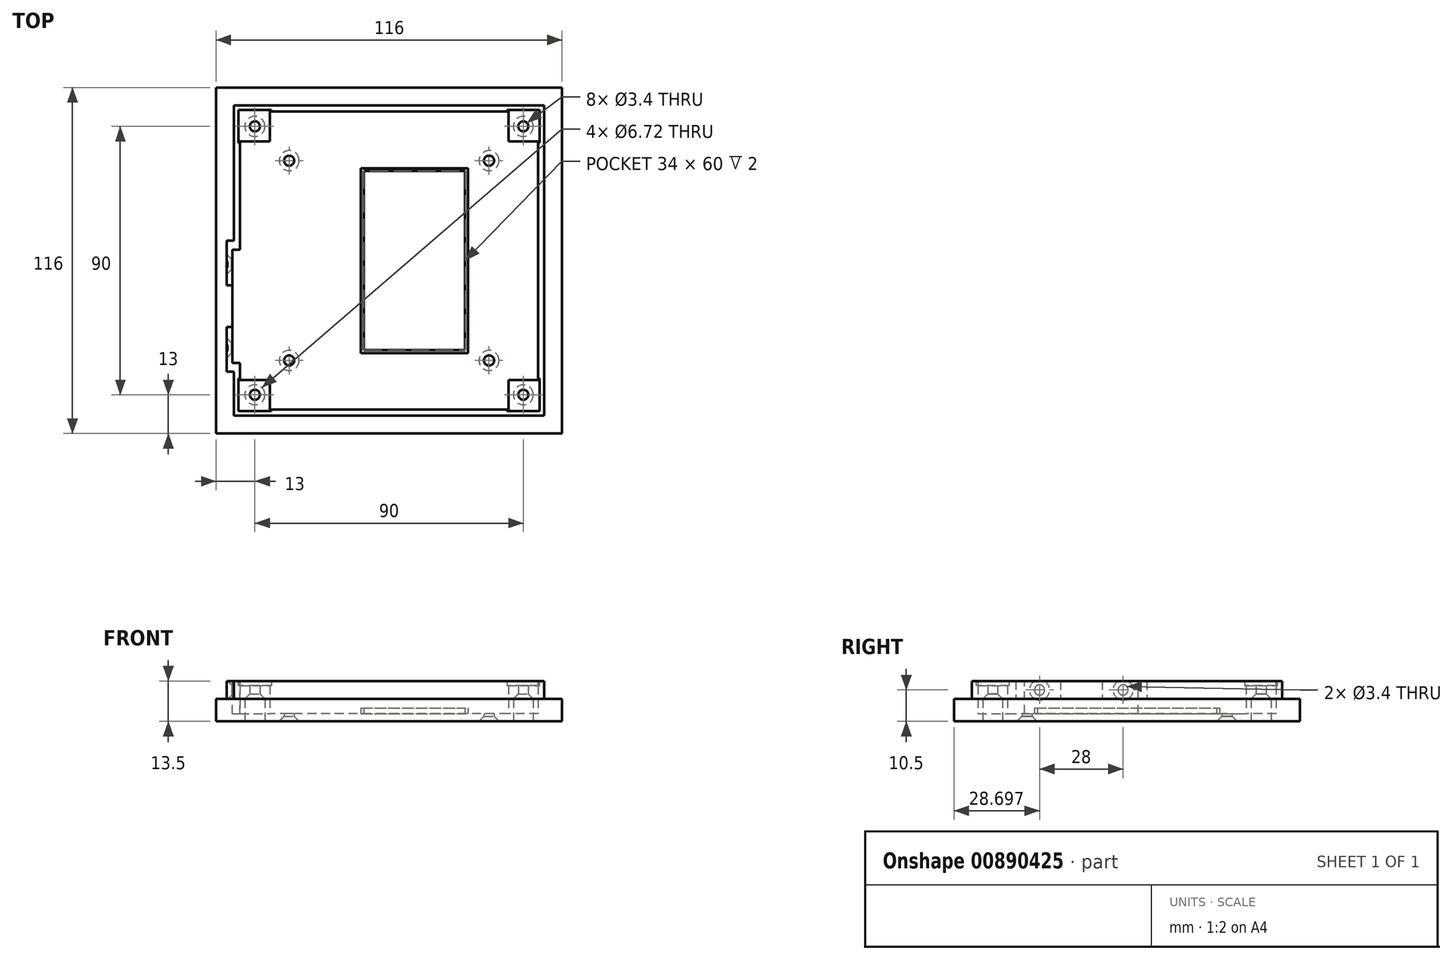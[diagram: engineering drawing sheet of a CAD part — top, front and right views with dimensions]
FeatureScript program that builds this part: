
annotation { "Feature Type Name" : "Feature", "Feature Type Description" : "" }
export const myFeature = defineFeature(function(context is Context, id is Id, definition is map)
    precondition{}
    {
        {
            var Q0;
            Q0=qCreatedBy(makeId("Top.planeOp"),FACE);
            var sketch = newSketch(context, id + "F0", { "sketchPlane" : qUnion([Q0])});
            skLineSegment(sketch, "E0.bottom", {"start": v(58, -58) * mm, "end": v(-58, -58) * mm});
            skLineSegment(sketch, "E0.top", {"start": v(58, 58) * mm, "end": v(-58, 58) * mm});
            skLineSegment(sketch, "E0.left", {"start": v(58, -58) * mm, "end": v(58, 58) * mm});
            skLineSegment(sketch, "E0.right", {"start": v(-58, -58) * mm, "end": v(-58, 58) * mm});
            skPoint(sketch, "E0.middle", {"position": v(0, 0) * mm});
            skSolve(sketch);
        }
        {
            var Q0;
            Q0 = qSketchRegion(id + "F0", true);
            extrude(context, id + "F1", {"entities" : qUnion([Q0]), "depth" : 13.5 * mm, "offsetDistance" : 25 * mm});
        }
        {
            var Q0;
            Q0=makeQuery(id+"F1.opExtrude","CAP_FACE",FACE,{"disambiguationData":[OSD([sQuery(id+"F0.wireOp",EDGE,"E0.bottom"),sQuery(id+"F0.wireOp",EDGE,"E0.top"),sQuery(id+"F0.wireOp",EDGE,"E0.left"),sQuery(id+"F0.wireOp",EDGE,"E0.right")])],"isStart":false});
            var sketch = newSketch(context, id + "F2", { "sketchPlane" : qUnion([Q0])});
            skLineSegment(sketch, "E1.bottom", {"start": v(58, -58) * mm, "end": v(-58, -58) * mm});
            skLineSegment(sketch, "E1.top", {"start": v(58, 58) * mm, "end": v(-58, 58) * mm});
            skLineSegment(sketch, "E1.left", {"start": v(58, -58) * mm, "end": v(58, 58) * mm});
            skLineSegment(sketch, "E1.right", {"start": v(-58, -58) * mm, "end": v(-58, 58) * mm});
            skPoint(sketch, "E1.middle", {"position": v(0, 0) * mm});
            skLineSegment(sketch, "E2.0", {"start": v(52, 52) * mm, "end": v(-52, 52) * mm});
            skLineSegment(sketch, "E2.1", {"start": v(52, -52) * mm, "end": v(52, 52) * mm});
            skLineSegment(sketch, "E2.2", {"start": v(52, -52) * mm, "end": v(-52, -52) * mm});
            skLineSegment(sketch, "E2.3", {"start": v(-52, -52) * mm, "end": v(-52, 52) * mm});
            skSolve(sketch);
        }
        {
            var Q0;
            Q0 = qSketchRegion(id + "F2", true);
            extrude(context, id + "F3", {"entities" : qUnion([Q0]), "operationType" : NewBodyOperationType.REMOVE, "oppositeDirection" : true, "depth" : 6 * mm, "offsetDistance" : 25 * mm});
        }
        {
            var Q0;
            Q0=makeQuery(id+"F1.opExtrude","CAP_FACE",FACE,{"disambiguationData":[OSD([sQuery(id+"F0.wireOp",EDGE,"E0.bottom"),sQuery(id+"F0.wireOp",EDGE,"E0.top"),sQuery(id+"F0.wireOp",EDGE,"E0.left"),sQuery(id+"F0.wireOp",EDGE,"E0.right")])],"isStart":false});
            var sketch = newSketch(context, id + "F4", { "sketchPlane" : qUnion([Q0])});
            skLineSegment(sketch, "E3.bottom", {"start": v(52, -52) * mm, "end": v(-52, -52) * mm});
            skLineSegment(sketch, "E3.top", {"start": v(52, 52) * mm, "end": v(-52, 52) * mm});
            skLineSegment(sketch, "E3.left", {"start": v(52, -52) * mm, "end": v(52, 52) * mm});
            skLineSegment(sketch, "E3.right", {"start": v(-52, -52) * mm, "end": v(-52, 52) * mm});
            skPoint(sketch, "E3.middle", {"position": v(0, 0) * mm});
            skLineSegment(sketch, "E4.0", {"start": v(50, 50) * mm, "end": v(-50, 50) * mm});
            skLineSegment(sketch, "E4.1", {"start": v(50, -50) * mm, "end": v(50, 50) * mm});
            skLineSegment(sketch, "E4.2", {"start": v(50, -50) * mm, "end": v(-50, -50) * mm});
            skLineSegment(sketch, "E4.3", {"start": v(-50, -50) * mm, "end": v(-50, 50) * mm});
            skSolve(sketch);
        }
        {
            var Q0;
            Q0=makeQuery(id+"F4.imprint","IMPRINT",FACE,{"disambiguationData":[TD([[makeQuery(id+"F4.imprint","IMPRINT",EDGE,{"derivedFrom":sQuery(id+"F4.wireOp",EDGE,"E4.0")}),1.0]])]});
            extrude(context, id + "F5", {"entities" : qUnion([Q0]), "operationType" : NewBodyOperationType.REMOVE, "oppositeDirection" : true, "depth" : 11 * mm, "offsetDistance" : 25 * mm});
        }
        {
            var Q0;
            Q0=makeQuery(id+"F5.boolean.opBoolean","COPY",FACE,{"derivedFrom":makeQuery(id+"F5.opExtrude","CAP_FACE",FACE,{"disambiguationData":[OSD([sQuery(id+"F4.wireOp",EDGE,"E4.0"),sQuery(id+"F4.wireOp",EDGE,"E4.1"),sQuery(id+"F4.wireOp",EDGE,"E4.2"),sQuery(id+"F4.wireOp",EDGE,"E4.3")])],"isStart":false})});
            var sketch = newSketch(context, id + "F6", { "sketchPlane" : qUnion([Q0])});
            skLineSegment(sketch, "E5.0", {"start": v(-45, 45) * mm, "end": v(45, 45) * mm, "construction": true});
            skLineSegment(sketch, "E5.1", {"start": v(-45, 45) * mm, "end": v(-45, -45) * mm, "construction": true});
            skLineSegment(sketch, "E5.2", {"start": v(-45, -45) * mm, "end": v(45, -45) * mm, "construction": true});
            skLineSegment(sketch, "E5.3", {"start": v(45, 45) * mm, "end": v(45, -45) * mm, "construction": true});
            skLineSegment(sketch, "E6.bottom", {"start": v(-50, 50) * mm, "end": v(-40, 50) * mm});
            skLineSegment(sketch, "E6.top", {"start": v(-50, 40) * mm, "end": v(-40, 40) * mm});
            skLineSegment(sketch, "E6.left", {"start": v(-50, 50) * mm, "end": v(-50, 40) * mm});
            skLineSegment(sketch, "E6.right", {"start": v(-40, 50) * mm, "end": v(-40, 40) * mm});
            skPoint(sketch, "E6.middle", {"position": v(-45, 45) * mm});
            skLineSegment(sketch, "E7.bottom", {"start": v(50, 50) * mm, "end": v(40, 50) * mm});
            skLineSegment(sketch, "E7.top", {"start": v(50, 40) * mm, "end": v(40, 40) * mm});
            skLineSegment(sketch, "E7.left", {"start": v(50, 50) * mm, "end": v(50, 40) * mm});
            skLineSegment(sketch, "E7.right", {"start": v(40, 50) * mm, "end": v(40, 40) * mm});
            skPoint(sketch, "E7.middle", {"position": v(45, 45) * mm});
            skLineSegment(sketch, "E8.bottom", {"start": v(50, -50) * mm, "end": v(40, -50) * mm});
            skLineSegment(sketch, "E8.top", {"start": v(50, -40) * mm, "end": v(40, -40) * mm});
            skLineSegment(sketch, "E8.left", {"start": v(50, -50) * mm, "end": v(50, -40) * mm});
            skLineSegment(sketch, "E8.right", {"start": v(40, -50) * mm, "end": v(40, -40) * mm});
            skPoint(sketch, "E8.middle", {"position": v(45, -45) * mm});
            skLineSegment(sketch, "E9.bottom", {"start": v(-50, -50) * mm, "end": v(-40, -50) * mm});
            skLineSegment(sketch, "E9.top", {"start": v(-50, -40) * mm, "end": v(-40, -40) * mm});
            skLineSegment(sketch, "E9.left", {"start": v(-50, -50) * mm, "end": v(-50, -40) * mm});
            skLineSegment(sketch, "E9.right", {"start": v(-40, -50) * mm, "end": v(-40, -40) * mm});
            skPoint(sketch, "E9.middle", {"position": v(-45, -45) * mm});
            skSolve(sketch);
        }
        {
            var Q0;
            Q0 = qSketchRegion(id + "F6", true);
            var Q1;
            Q1=makeQuery(id+"F1.opExtrude","CAP_FACE",FACE,{"disambiguationData":[OSD([sQuery(id+"F0.wireOp",EDGE,"E0.bottom"),sQuery(id+"F0.wireOp",EDGE,"E0.top"),sQuery(id+"F0.wireOp",EDGE,"E0.left"),sQuery(id+"F0.wireOp",EDGE,"E0.right")])],"isStart":false});
            extrude(context, id + "F7", {"entities" : qUnion([Q0]), "operationType" : NewBodyOperationType.ADD, "endBound" : BoundingType.UP_TO_SURFACE, "depth" : 9.5 * mm, "endBoundEntityFace" : qUnion([Q1]), "hasOffset" : true, "offsetDistance" : 1.5 * mm});
        }
        {
            var Q0;
            Q0=makeQuery(id+"F1.opExtrude","CAP_FACE",FACE,{"disambiguationData":[OSD([sQuery(id+"F0.wireOp",EDGE,"E0.bottom"),sQuery(id+"F0.wireOp",EDGE,"E0.top"),sQuery(id+"F0.wireOp",EDGE,"E0.left"),sQuery(id+"F0.wireOp",EDGE,"E0.right")])],"isStart":true});
            var sketch = newSketch(context, id + "F8", { "sketchPlane" : qUnion([Q0])});
            skLineSegment(sketch, "E10.0", {"start": v(45, 45) * mm, "end": v(-45, 45) * mm, "construction": true});
            skLineSegment(sketch, "E10.1", {"start": v(45, 45) * mm, "end": v(45, -45) * mm, "construction": true});
            skLineSegment(sketch, "E10.2", {"start": v(45, -45) * mm, "end": v(-45, -45) * mm, "construction": true});
            skLineSegment(sketch, "E10.3", {"start": v(-45, 45) * mm, "end": v(-45, -45) * mm, "construction": true});
            skCircle(sketch, "E11", {"center": v(-45, 45) * mm, "radius": 3.36 * mm});
            skCircle(sketch, "E12", {"center": v(45, 45) * mm, "radius": 3.36 * mm});
            skCircle(sketch, "E13", {"center": v(-45, -45) * mm, "radius": 3.36 * mm});
            skCircle(sketch, "E14", {"center": v(45, -45) * mm, "radius": 3.36 * mm});
            skSolve(sketch);
        }
        {
            var Q0;
            Q0 = qSketchRegion(id + "F8", true);
            var Q1;
            Q1=makeQuery(id+"F7.opExtrude","CAP_FACE",FACE,{"disambiguationData":[OSD([sQuery(id+"F6.wireOp",EDGE,"E9.bottom"),sQuery(id+"F6.wireOp",EDGE,"E9.top"),sQuery(id+"F6.wireOp",EDGE,"E9.left"),sQuery(id+"F6.wireOp",EDGE,"E9.right")])],"isStart":false});
            extrude(context, id + "F9", {"entities" : qUnion([Q0]), "operationType" : NewBodyOperationType.REMOVE, "oppositeDirection" : true, "depth" : 7.5 * mm, "endBoundEntityFace" : qUnion([Q1]), "hasOffset" : true, "offsetDistance" : 5 * mm});
        }
        {
            var Q0;
            Q0=makeQuery(id+"F3.boolean.opBoolean","COPY",FACE,{"derivedFrom":makeQuery(id+"F3.opExtrude","CAP_FACE",FACE,{"disambiguationData":[OSD([sQuery(id+"F2.wireOp",EDGE,"E1.bottom"),sQuery(id+"F2.wireOp",EDGE,"E1.top"),sQuery(id+"F2.wireOp",EDGE,"E1.left"),sQuery(id+"F2.wireOp",EDGE,"E1.right"),sQuery(id+"F2.wireOp",EDGE,"E2.0"),sQuery(id+"F2.wireOp",EDGE,"E2.1"),sQuery(id+"F2.wireOp",EDGE,"E2.2"),sQuery(id+"F2.wireOp",EDGE,"E2.3")])],"isStart":false})});
            var sketch = newSketch(context, id + "F10", { "sketchPlane" : qUnion([Q0])});
            skLineSegment(sketch, "E15.0", {"start": v(45, -45) * mm, "end": v(-45, -45) * mm, "construction": true});
            skLineSegment(sketch, "E15.1", {"start": v(45, -45) * mm, "end": v(45, 45) * mm, "construction": true});
            skLineSegment(sketch, "E15.2", {"start": v(45, 45) * mm, "end": v(-45, 45) * mm, "construction": true});
            skLineSegment(sketch, "E15.3", {"start": v(-45, -45) * mm, "end": v(-45, 45) * mm, "construction": true});
            skSolve(sketch);
        }
        {
            var Q0;
            Q0=sQuery(id+"F10.wireOp",VERTEX,"E15.0.end");
            var Q1;
            Q1=sQuery(id+"F10.wireOp",VERTEX,"E15.0.start");
            var Q2;
            Q2=sQuery(id+"F10.wireOp",VERTEX,"E15.1.end");
            var Q3;
            Q3=sQuery(id+"F10.wireOp",VERTEX,"E15.2.end");
            var Q4;
            Q4=makeQuery(id+"F1.opExtrude","SWEPT_BODY",BODY,{"disambiguationData":[OSD([sQuery(id+"F0.wireOp",EDGE,"E0.bottom"),sQuery(id+"F0.wireOp",EDGE,"E0.top"),sQuery(id+"F0.wireOp",EDGE,"E0.left"),sQuery(id+"F0.wireOp",EDGE,"E0.right")])]});
            hole(context, id + "F11", {"style" : HoleStyle.C_SINK, "endStyle" : HoleEndStyle.THROUGH, "oppositeDirection" : true, "standardTappedOrClearance" : lookupTablePath({ "fit" : "Normal", "standard" : "ISO", "size" : "M3", "type" : "Clearance" }), "standardBlindInLast" : lookupTablePath({ "fit" : "Normal", "standard" : "ISO", "size" : "M3", "type" : "Clearance" }), "holeDiameter" : 3.4 * mm, "cSinkDiameter" : 6.72 * mm, "cSinkAngle" : 90 * degree, "majorDiameter" : 5 * mm, "isTappedThrough" : true, "tappedDepth" : 12 * mm, "tapClearance" : 3, "locations" : qUnion([Q0, Q1, Q2, Q3]), "scope" : qUnion([Q4])});
        }
        {
            var Q0;
            Q0=makeQuery(id+"F1.opExtrude","CAP_FACE",FACE,{"disambiguationData":[OSD([sQuery(id+"F0.wireOp",EDGE,"E0.bottom"),sQuery(id+"F0.wireOp",EDGE,"E0.top"),sQuery(id+"F0.wireOp",EDGE,"E0.left"),sQuery(id+"F0.wireOp",EDGE,"E0.right")])],"isStart":true});
            var sketch = newSketch(context, id + "F12", { "sketchPlane" : qUnion([Q0])});
            skLineSegment(sketch, "E16.bottom", {"start": v(33.5, -33.5) * mm, "end": v(-33.5, -33.5) * mm, "construction": true});
            skLineSegment(sketch, "E16.top", {"start": v(33.5, 33.5) * mm, "end": v(-33.5, 33.5) * mm, "construction": true});
            skLineSegment(sketch, "E16.left", {"start": v(33.5, -33.5) * mm, "end": v(33.5, 33.5) * mm, "construction": true});
            skLineSegment(sketch, "E16.right", {"start": v(-33.5, -33.5) * mm, "end": v(-33.5, 33.5) * mm, "construction": true});
            skPoint(sketch, "E16.middle", {"position": v(0, 0) * mm});
            skSolve(sketch);
        }
        {
            var Q0;
            Q0=sQuery(id+"F12.wireOp",VERTEX,"E16.top.end");
            var Q1;
            Q1=sQuery(id+"F12.wireOp",VERTEX,"E16.top.start");
            var Q2;
            Q2=sQuery(id+"F12.wireOp",VERTEX,"E16.bottom.start");
            var Q3;
            Q3=sQuery(id+"F12.wireOp",VERTEX,"E16.bottom.end");
            var Q4;
            Q4=makeQuery(id+"F1.opExtrude","SWEPT_BODY",BODY,{"disambiguationData":[OSD([sQuery(id+"F0.wireOp",EDGE,"E0.bottom"),sQuery(id+"F0.wireOp",EDGE,"E0.top"),sQuery(id+"F0.wireOp",EDGE,"E0.left"),sQuery(id+"F0.wireOp",EDGE,"E0.right")])]});
            hole(context, id + "F13", {"style" : HoleStyle.C_SINK, "endStyle" : HoleEndStyle.THROUGH, "standardTappedOrClearance" : lookupTablePath({ "fit" : "Normal", "standard" : "ISO", "size" : "M3", "type" : "Clearance" }), "standardBlindInLast" : lookupTablePath({ "fit" : "Normal", "standard" : "ISO", "size" : "M3", "type" : "Clearance" }), "holeDiameter" : 3.4 * mm, "cSinkDiameter" : 6.72 * mm, "cSinkAngle" : 90 * degree, "majorDiameter" : 5 * mm, "isTappedThrough" : true, "tappedDepth" : 12 * mm, "tapClearance" : 3, "locations" : qUnion([Q0, Q1, Q2, Q3]), "scope" : qUnion([Q4])});
        }
        {
            var Q0;
            Q0=makeQuery(id+"F5.boolean.opBoolean","COPY",FACE,{"derivedFrom":makeQuery(id+"F5.opExtrude","CAP_FACE",FACE,{"disambiguationData":[OSD([sQuery(id+"F4.wireOp",EDGE,"E4.0"),sQuery(id+"F4.wireOp",EDGE,"E4.1"),sQuery(id+"F4.wireOp",EDGE,"E4.2"),sQuery(id+"F4.wireOp",EDGE,"E4.3")])],"isStart":false})});
            var sketch = newSketch(context, id + "F14", { "sketchPlane" : qUnion([Q0])});
            skLineSegment(sketch, "E17.bottom", {"start": v(-8.5, -30) * mm, "end": v(8.5, -30) * mm});
            skLineSegment(sketch, "E17.top", {"start": v(-8.5, 30) * mm, "end": v(8.5, 30) * mm});
            skLineSegment(sketch, "E17.left", {"start": v(-8.5, -30) * mm, "end": v(-8.5, 30) * mm});
            skPoint(sketch, "E17.middle", {"position": v(0, 0) * mm});
            skLineSegment(sketch, "E18", {"start": v(8.5, 30) * mm, "end": v(25.5, 30) * mm});
            skLineSegment(sketch, "E19", {"start": v(25.5, 30) * mm, "end": v(25.5, -30) * mm});
            skLineSegment(sketch, "E20", {"start": v(25.5, -30) * mm, "end": v(8.5, -30) * mm});
            skLineSegment(sketch, "E21.0", {"start": v(-9.5, -31) * mm, "end": v(-9.5, 31) * mm});
            skLineSegment(sketch, "E21.1", {"start": v(8.5, 31) * mm, "end": v(26.5, 31) * mm});
            skLineSegment(sketch, "E21.2", {"start": v(26.5, 31) * mm, "end": v(26.5, -31) * mm});
            skLineSegment(sketch, "E21.3", {"start": v(-9.5, 31) * mm, "end": v(8.5, 31) * mm});
            skLineSegment(sketch, "E21.4", {"start": v(26.5, -31) * mm, "end": v(8.5, -31) * mm});
            skLineSegment(sketch, "E21.5", {"start": v(-9.5, -31) * mm, "end": v(8.5, -31) * mm});
            skSolve(sketch);
        }
        {
            var Q0;
            Q0 = qSketchRegion(id + "F14", true);
            extrude(context, id + "F15", {"entities" : qUnion([Q0]), "operationType" : NewBodyOperationType.ADD, "depth" : 2 * mm, "offsetDistance" : 25 * mm});
        }
        {
            var Q0;
            {var subQ0=sQuery(id+"F2.wireOp",EDGE,"E2.0");var subQ1=sQuery(id+"F2.wireOp",EDGE,"E2.3");Q0=makeQuery(id+"F3LvmwCe6z8T8Rk_1.boolean.opBoolean","SPLIT",FACE,{"disambiguationData":[TD([makeQuery(id+"F3.boolean.opBoolean","COPY",FACE,{"derivedFrom":makeQuery(id+"F3.opExtrude","SWEPT_FACE",FACE,{"disambiguationData":[OSD([subQ0])]})})])],"derivedFrom":makeQuery(id+"F3.boolean.opBoolean","COPY",FACE,{"derivedFrom":makeQuery(id+"F3.opExtrude","SWEPT_FACE",FACE,{"disambiguationData":[OSD([subQ1])]})})});}
            var sketch = newSketch(context, id + "F16", { "sketchPlane" : qUnion([Q0])});
            skLineSegment(sketch, "E22.bottom", {"start": v(8.3, 13.5) * mm, "end": v(-6.7, 13.5) * mm});
            skLineSegment(sketch, "E22.top", {"start": v(8.3, 7.5) * mm, "end": v(-6.7, 7.5) * mm});
            skLineSegment(sketch, "E22.left", {"start": v(8.3, 13.5) * mm, "end": v(8.3, 7.5) * mm});
            skLineSegment(sketch, "E22.right", {"start": v(-6.7, 13.5) * mm, "end": v(-6.7, 7.5) * mm});
            skLineSegment(sketch, "E23.bottom", {"start": v(22.3, 13.5) * mm, "end": v(37.3, 13.5) * mm});
            skLineSegment(sketch, "E23.top", {"start": v(22.3, 7.5) * mm, "end": v(37.3, 7.5) * mm});
            skLineSegment(sketch, "E23.left", {"start": v(22.3, 13.5) * mm, "end": v(22.3, 7.5) * mm});
            skLineSegment(sketch, "E23.right", {"start": v(37.3, 13.5) * mm, "end": v(37.3, 7.5) * mm});
            skSolve(sketch);
        }
        {
            var Q0;
            Q0 = qSketchRegion(id + "F16", true);
            extrude(context, id + "F17", {"entities" : qUnion([Q0]), "operationType" : NewBodyOperationType.ADD, "depth" : 2.5 * mm, "offsetDistance" : 25 * mm});
        }
        {
            var Q0;
            Q0=makeQuery(id+"F17.boolean.opBoolean","MERGE",FACE,{"derivedFrom":[makeQuery(id+"F1.opExtrude","CAP_FACE",FACE,{"disambiguationData":[OSD([sQuery(id+"F0.wireOp",EDGE,"E0.bottom"),sQuery(id+"F0.wireOp",EDGE,"E0.top"),sQuery(id+"F0.wireOp",EDGE,"E0.left"),sQuery(id+"F0.wireOp",EDGE,"E0.right")])],"isStart":false}),makeQuery(id+"F17.opExtrude","SWEPT_FACE",FACE,{"disambiguationData":[OSD([sQuery(id+"F16.wireOp",EDGE,"E22.bottom")])]}),makeQuery(id+"F17.opExtrude","SWEPT_FACE",FACE,{"disambiguationData":[OSD([sQuery(id+"F16.wireOp",EDGE,"E23.bottom")])]})]});
            var sketch = newSketch(context, id + "F18", { "sketchPlane" : qUnion([Q0])});
            skLineSegment(sketch, "E24.top", {"start": v(-50, 3.7) * mm, "end": v(-52.5, 3.7) * mm});
            skLineSegment(sketch, "E24.left", {"start": v(-50, -8.3) * mm, "end": v(-50, 3.7) * mm});
            skLineSegment(sketch, "E24.right", {"start": v(-52.5, -8.3) * mm, "end": v(-52.5, 3.7) * mm});
            skLineSegment(sketch, "E25.top", {"start": v(-50, -34.3) * mm, "end": v(-52.5, -34.3) * mm});
            skLineSegment(sketch, "E25.left", {"start": v(-50, -22.3) * mm, "end": v(-50, -34.3) * mm});
            skLineSegment(sketch, "E25.right", {"start": v(-52.5, -22.3) * mm, "end": v(-52.5, -34.3) * mm});
            skLineSegment(sketch, "E26", {"start": v(-52.5, -22.3) * mm, "end": v(-52.5, -8.3) * mm});
            skLineSegment(sketch, "E27", {"start": v(-50, -8.3) * mm, "end": v(-50, -22.3) * mm});
            skSolve(sketch);
        }
        {
            var Q0;
            Q0 = qSketchRegion(id + "F18", true);
            var Q1;
            {var subQ0=sQuery(id+"F4.wireOp",EDGE,"E4.0");var subQ1=sQuery(id+"F4.wireOp",EDGE,"E4.1");var subQ2=sQuery(id+"F4.wireOp",EDGE,"E4.2");var subQ3=sQuery(id+"F4.wireOp",EDGE,"E4.3");Q1=makeQuery(id+"F15.boolean.opBoolean","SPLIT",FACE,{"disambiguationData":[TD([makeQuery(id+"F5.boolean.opBoolean","COPY",FACE,{"derivedFrom":makeQuery(id+"F5.opExtrude","SWEPT_FACE",FACE,{"disambiguationData":[OSD([subQ0])]})})])],"derivedFrom":makeQuery(id+"F5.boolean.opBoolean","COPY",FACE,{"derivedFrom":makeQuery(id+"F5.opExtrude","CAP_FACE",FACE,{"disambiguationData":[OSD([subQ0,subQ1,subQ2,subQ3])],"isStart":false})})});}
            extrude(context, id + "F19", {"entities" : qUnion([Q0]), "operationType" : NewBodyOperationType.REMOVE, "endBound" : BoundingType.UP_TO_SURFACE, "oppositeDirection" : true, "depth" : 25 * mm, "endBoundEntityFace" : qUnion([Q1]), "offsetDistance" : 25 * mm});
        }
        {
            var Q0;
            Q0=makeQuery(id+"F17.opExtrude","CAP_FACE",FACE,{"disambiguationData":[OSD([sQuery(id+"F16.wireOp",EDGE,"E22.bottom"),sQuery(id+"F16.wireOp",EDGE,"E22.top"),sQuery(id+"F16.wireOp",EDGE,"E22.left"),sQuery(id+"F16.wireOp",EDGE,"E22.right")])],"isStart":false});
            var sketch = newSketch(context, id + "F20", { "sketchPlane" : qUnion([Q0])});
            skCircle(sketch, "E28", {"center": v(1.3, 10.5) * mm, "radius": 1.5 * mm});
            skCircle(sketch, "E29", {"center": v(29.3, 10.5) * mm, "radius": 1.5 * mm});
            skSolve(sketch);
        }
        {
            var Q0;
            Q0=sQuery(id+"F20.wireOp",VERTEX,"E28.center");
            var Q1;
            Q1=sQuery(id+"F20.wireOp",VERTEX,"E29.center");
            var Q2;
            Q2=makeQuery(id+"F1.opExtrude","SWEPT_BODY",BODY,{"disambiguationData":[OSD([sQuery(id+"F0.wireOp",EDGE,"E0.bottom"),sQuery(id+"F0.wireOp",EDGE,"E0.top"),sQuery(id+"F0.wireOp",EDGE,"E0.left"),sQuery(id+"F0.wireOp",EDGE,"E0.right")])]});
            hole(context, id + "F21", {"style" : HoleStyle.C_SINK, "endStyle" : HoleEndStyle.BLIND, "holeDiameter" : 3.4 * mm, "cSinkDiameter" : 6.72 * mm, "cSinkAngle" : 90 * degree, "majorDiameter" : 5 * mm, "holeDepth" : 12 * mm, "isTappedThrough" : true, "tappedDepth" : 12 * mm, "tapClearance" : 3, "locations" : qUnion([Q0, Q1]), "scope" : qUnion([Q2])});
        }
        {
            var Q0;
            Q0=makeQuery(id+"F17.boolean.opBoolean","MERGE",FACE,{"derivedFrom":[makeQuery(id+"F1.opExtrude","CAP_FACE",FACE,{"disambiguationData":[OSD([sQuery(id+"F0.wireOp",EDGE,"E0.bottom"),sQuery(id+"F0.wireOp",EDGE,"E0.top"),sQuery(id+"F0.wireOp",EDGE,"E0.left"),sQuery(id+"F0.wireOp",EDGE,"E0.right")])],"isStart":false}),makeQuery(id+"F17.opExtrude","SWEPT_FACE",FACE,{"disambiguationData":[OSD([sQuery(id+"F16.wireOp",EDGE,"E22.bottom")])]}),makeQuery(id+"F17.opExtrude","SWEPT_FACE",FACE,{"disambiguationData":[OSD([sQuery(id+"F16.wireOp",EDGE,"E23.bottom")])]})]});
            var sketch = newSketch(context, id + "F22", { "sketchPlane" : qUnion([Q0])});
            skLineSegment(sketch, "E30.0", {"start": v(-50.5, 50.5) * mm, "end": v(-50.5, 39.5) * mm});
            skLineSegment(sketch, "E30.1", {"start": v(-50.5, 50.5) * mm, "end": v(-39.5, 50.5) * mm});
            skLineSegment(sketch, "E30.2", {"start": v(-39.5, 50.5) * mm, "end": v(-39.5, 39.5) * mm});
            skLineSegment(sketch, "E30.3", {"start": v(-50.5, 39.5) * mm, "end": v(-39.5, 39.5) * mm});
            skLineSegment(sketch, "E31.0", {"start": v(50.5, 50.5) * mm, "end": v(39.5, 50.5) * mm});
            skLineSegment(sketch, "E31.1", {"start": v(50.5, 50.5) * mm, "end": v(50.5, 39.5) * mm});
            skLineSegment(sketch, "E31.2", {"start": v(50.5, 39.5) * mm, "end": v(39.5, 39.5) * mm});
            skLineSegment(sketch, "E31.3", {"start": v(39.5, 50.5) * mm, "end": v(39.5, 39.5) * mm});
            skLineSegment(sketch, "E32.0", {"start": v(50.5, -39.5) * mm, "end": v(39.5, -39.5) * mm});
            skLineSegment(sketch, "E32.1", {"start": v(50.5, -50.5) * mm, "end": v(50.5, -39.5) * mm});
            skLineSegment(sketch, "E32.2", {"start": v(50.5, -50.5) * mm, "end": v(39.5, -50.5) * mm});
            skLineSegment(sketch, "E32.3", {"start": v(39.5, -50.5) * mm, "end": v(39.5, -39.5) * mm});
            skLineSegment(sketch, "E33.0", {"start": v(-50.5, -39.5) * mm, "end": v(-39.5, -39.5) * mm});
            skLineSegment(sketch, "E33.1", {"start": v(-50.5, -50.5) * mm, "end": v(-50.5, -39.5) * mm});
            skLineSegment(sketch, "E33.2", {"start": v(-50.5, -50.5) * mm, "end": v(-39.5, -50.5) * mm});
            skLineSegment(sketch, "E33.3", {"start": v(-39.5, -50.5) * mm, "end": v(-39.5, -39.5) * mm});
            skSolve(sketch);
        }
        {
            var Q0;
            Q0 = qSketchRegion(id + "F22", true);
            var Q1;
            Q1=makeQuery(id+"F7.opExtrude","CAP_FACE",FACE,{"disambiguationData":[OSD([sQuery(id+"F6.wireOp",EDGE,"E6.bottom"),sQuery(id+"F6.wireOp",EDGE,"E6.top"),sQuery(id+"F6.wireOp",EDGE,"E6.left"),sQuery(id+"F6.wireOp",EDGE,"E6.right")])],"isStart":false});
            extrude(context, id + "F23", {"entities" : qUnion([Q0]), "operationType" : NewBodyOperationType.REMOVE, "endBound" : BoundingType.UP_TO_SURFACE, "oppositeDirection" : true, "depth" : 25 * mm, "endBoundEntityFace" : qUnion([Q1]), "offsetDistance" : 25 * mm});
        }
    });
